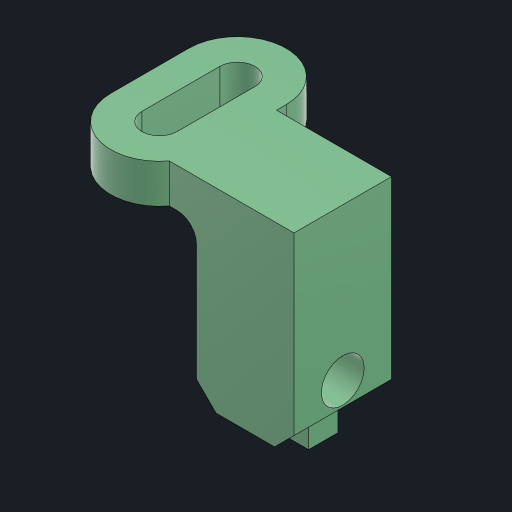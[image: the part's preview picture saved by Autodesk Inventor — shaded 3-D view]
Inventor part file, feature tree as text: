
AUTODESK INVENTOR PART (.ipt)
format: ipt  version: 2023 (Build 270158000, 158)  size: 196,608 bytes
history: native  units: mm
features: sketch x3, extrude x3, other x2, hole x1, fillet x1, chamfer x1
ambient origin geometry x8: Origin, YZ Plane, XZ Plane, XY Plane, X Axis, Y Axis, Z Axis, Center Point
bodies: Body1 (feature_tree)
feature tree (11):
  other  "ソリッド1"
  sketch  "スケッチ1"
  extrude  "押し出し1"  Depth=1.8mm
  extrude  "押し出し4"  Depth=4.0mm
  hole  "穴3"  [1 undecoded]
  fillet  "フィレット3"  Radius=2.0mm
  other  "作業平面2"
  chamfer  "面取り1"  Distance=8.0mm
  extrude  "押し出し5"  Depth=5.0mm
  sketch  "スケッチ6"
  sketch  "スケッチ7"
note: 1 required parameter value undecoded (feature->parameter linkage not recoverable at this tier; creation-order binding heuristic only, values carry confidence <= 0.55)
